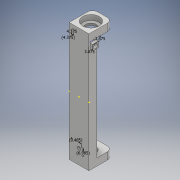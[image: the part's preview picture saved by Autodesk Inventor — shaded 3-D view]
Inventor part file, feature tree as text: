
AUTODESK INVENTOR PART (.ipt)
format: ipt  version: 2018 (Build 220112000, 112)  size: 265,216 bytes
history: native  units: mm
features: sketch x21, extrude x12, fillet x3
ambient origin geometry x8: Origin, YZ Plane, XZ Plane, XY Plane, X Axis, Y Axis, Z Axis, Center Point
bodies: Solid1 (feature_tree)
feature tree (36):
  extrude  "Extrusion1"  Depth=100.0mm
  sketch  "Sketch2"  dims[d2=2.0mm d3=0.0mm d4=2.5mm]
  sketch  "Sketch3"  dims[d5=2.5mm d6=10.89mm d7=0.0mm]
  extrude  "Extrusion2"  Depth=2.5mm
  extrude  "Extrusion3"  Depth=10.89mm TaperAngle=0.0deg
  extrude  "Extrusion4"  Depth=2.14mm TaperAngle=0.0deg
  extrude  "Extrusion5"  Depth=2.14mm TaperAngle=0.0deg
  fillet  "Fillet1"  Radius=7.0mm
  extrude  "Extrusion6"  Depth=22.5mm
  extrude  "Extrusion7"  Depth=7.0mm TaperAngle=0.0deg
  fillet  "Fillet2"  Radius=7.0mm
  extrude  "Extrusion8"  Depth=5.0mm
  extrude  "Extrusion9"  Depth=2.0mm TaperAngle=0.0deg
  sketch  "Sketch12"  dims[d35=2.0mm d36=6.985mm]
  extrude  "Extrusion10"  Depth=2.0mm TaperAngle=0.0deg
  fillet  "Fillet3"  Radius=13.97mm
  sketch  "Sketch14"  dims[d38=7.75mm]
  sketch  "Sketch15"  dims[d39=5.5mm]
  extrude  "Extrusion11"  Depth=2.0mm TaperAngle=0.0deg
  sketch  "Sketch17"  dims[d41=4.0mm]
  sketch  "Sketch18"  dims[d42=2.5mm d43=0.0mm]
  sketch  "Sketch19"  dims[d44=3.875mm]
  extrude  "Extrusion12"  Depth=2.0mm
  sketch  "Sketch21"  dims[d46=8.75mm d47=3.0mm d48=3.0mm d49=0.0mm d50=4.375mm d51=4.375mm]
  sketch  "Sketch1"  dims[d0=13.97mm d1=100.0mm]
  sketch  "Sketch4"  dims[d8=3.14mm d9=0.0mm d10=2.14mm d11=0.0mm]
  sketch  "Sketch5"  dims[d12=3.5mm d13=2.14mm d14=0.0mm d15=7.0mm]
  sketch  "Sketch6"  dims[d16=11.43mm d17=22.5mm]
  sketch  "Sketch7"  dims[d18=15.975mm d19=7.0mm d20=0.0mm d21=7.0mm d22=0.0mm]
  sketch  "Sketch8"  dims[d23=5.0mm d24=6.35mm]
  sketch  "Sketch9"  dims[d25=10.0mm d26=2.0mm d27=0.0mm]
  sketch  "Sketch10"  dims[d28=10.0mm d29=2.0mm d30=0.0mm d31=13.97mm]
  sketch  "Sketch11"  dims[d32=3.175mm d33=2.0mm d34=0.0mm]
  sketch  "Sketch13"  dims[d37=9.485mm]
  sketch  "Sketch16"  dims[d40=5.5mm]
  sketch  "Sketch20"  dims[d45=3.875mm]
